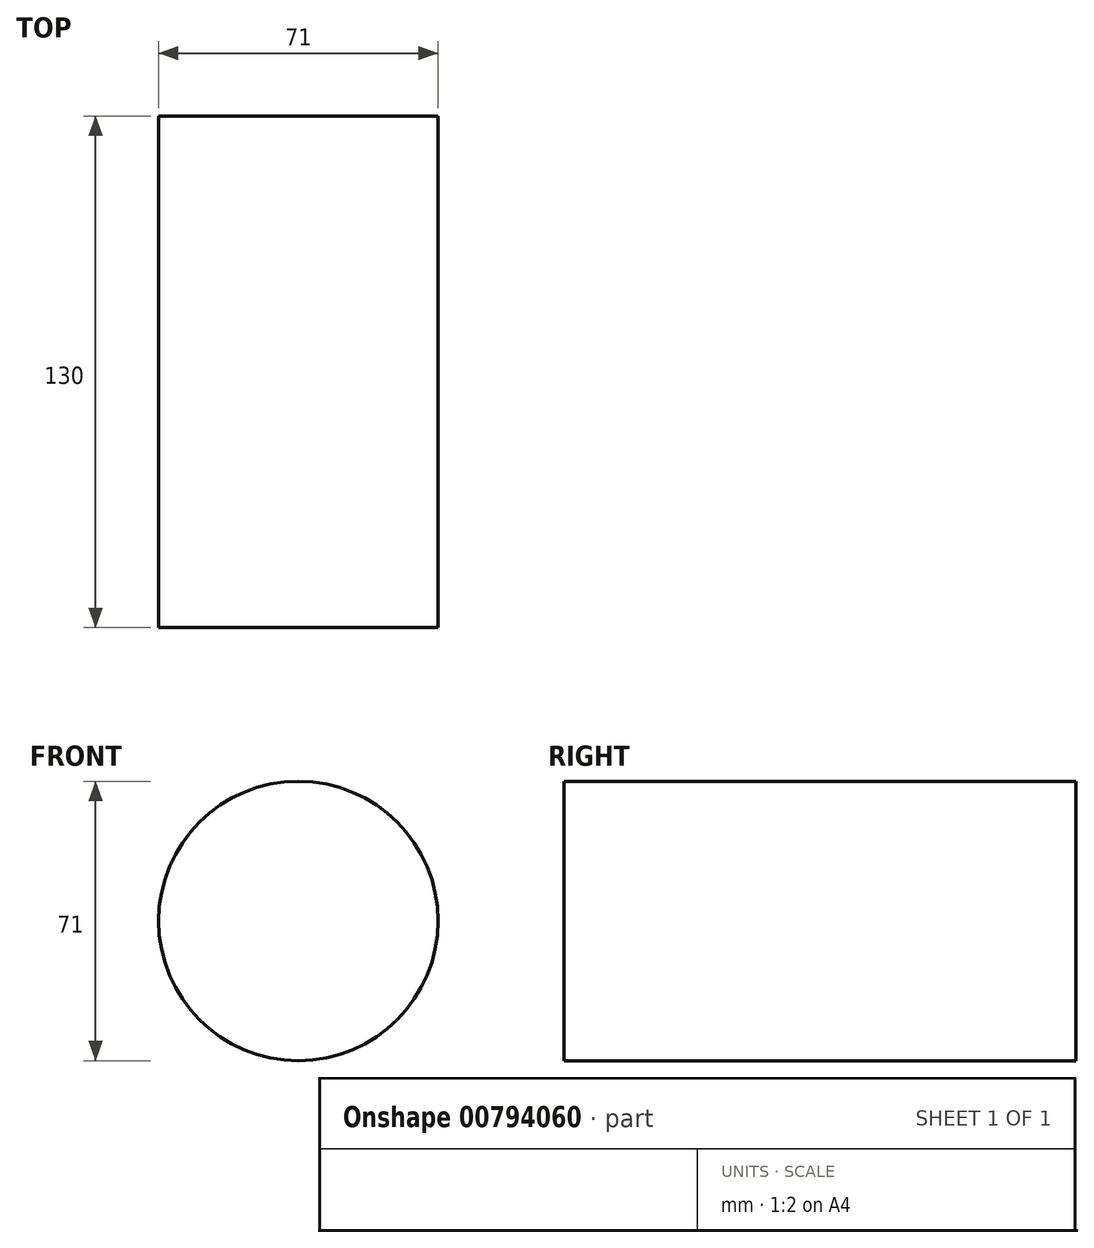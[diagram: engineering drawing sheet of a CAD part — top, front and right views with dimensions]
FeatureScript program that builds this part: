
annotation { "Feature Type Name" : "Feature", "Feature Type Description" : "" }
export const myFeature = defineFeature(function(context is Context, id is Id, definition is map)
    precondition{}
    {
        {
            var Q0;
            Q0=qCreatedBy(makeId("Front.planeOp"),FACE);
            var sketch = newSketch(context, id + "F0", { "sketchPlane" : qUnion([Q0])});
            skLineSegment(sketch, "E0", {"start": v(-36.48, 0) * mm, "end": v(-36.48, 25) * mm});
            skLineSegment(sketch, "E1", {"start": v(-36.48, 25) * mm, "end": v(-7.5, 25) * mm});
            skLineSegment(sketch, "E2", {"start": v(-7.5, 25) * mm, "end": v(-7.5, 60.3) * mm});
            skLineSegment(sketch, "E3", {"start": v(7.5, 60.04) * mm, "end": v(7.5, 25) * mm});
            skLineSegment(sketch, "E4", {"start": v(7.5, 25) * mm, "end": v(129.1, 25) * mm});
            skLineSegment(sketch, "E5", {"start": v(129.1, 25) * mm, "end": v(129.1, 35) * mm});
            skLineSegment(sketch, "E6", {"start": v(129.1, 35) * mm, "end": v(163.52, 35) * mm});
            skLineSegment(sketch, "E7", {"start": v(163.52, 35) * mm, "end": v(163.52, 0) * mm});
            skLineSegment(sketch, "E8", {"start": v(163.52, 0) * mm, "end": v(-36.48, 0) * mm});
            skLineSegment(sketch, "E9", {"start": v(0, 52.68) * mm, "end": v(0, -6.9) * mm, "construction": true});
            skLineSegment(sketch, "E10", {"start": v(-89.85, 0) * mm, "end": v(219.27, 0) * mm, "construction": true});
            skCircle(sketch, "E11", {"center": v(0, 95) * mm, "radius": 35.5 * mm});
            skSolve(sketch);
        }
        {
            var Q0;
            Q0 = qSketchRegion(id + "F0", true);
            extrude(context, id + "F1", {"entities" : qUnion([Q0]), "oppositeDirection" : true, "depth" : 130 * mm, "offsetDistance" : 25 * mm});
        }
    });
